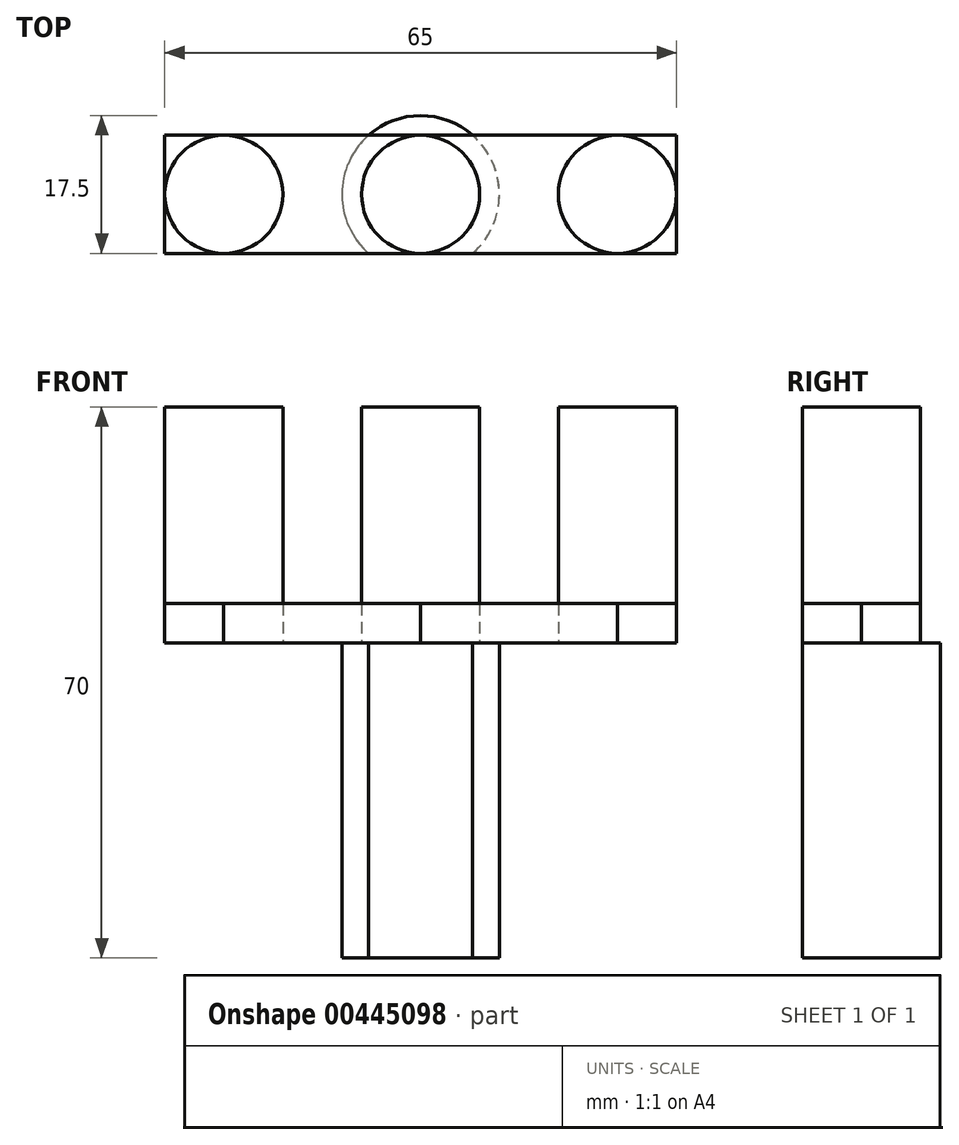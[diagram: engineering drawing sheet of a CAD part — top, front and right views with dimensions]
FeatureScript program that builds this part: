
annotation { "Feature Type Name" : "Feature", "Feature Type Description" : "" }
export const myFeature = defineFeature(function(context is Context, id is Id, definition is map)
    precondition{}
    {
        {
            var Q0;
            Q0=qCreatedBy(makeId("Top.planeOp"),FACE);
            var sketch = newSketch(context, id + "F0", { "sketchPlane" : qUnion([Q0])});
            skCircle(sketch, "E0", {"center": v(0, 0) * mm, "radius": 7.5 * mm});
            skCircle(sketch, "E1", {"center": v(-25, 0) * mm, "radius": 7.5 * mm});
            skCircle(sketch, "E2", {"center": v(25, 0) * mm, "radius": 7.5 * mm});
            skLineSegment(sketch, "E3.bottom", {"start": v(32.5, 7.5) * mm, "end": v(-32.5, 7.5) * mm});
            skLineSegment(sketch, "E3.top", {"start": v(32.5, -7.5) * mm, "end": v(-32.5, -7.5) * mm});
            skLineSegment(sketch, "E3.left", {"start": v(32.5, 7.5) * mm, "end": v(32.5, -7.5) * mm});
            skLineSegment(sketch, "E3.right", {"start": v(-32.5, 7.5) * mm, "end": v(-32.5, -7.5) * mm});
            skCircle(sketch, "E4", {"center": v(0, 0) * mm, "radius": 10 * mm});
            skSolve(sketch);
        }
        {
            var Q0;
            {var subQ0=sQuery(id+"F0.wireOp",EDGE,"E1");var subQ1=makeQuery(id+"F0.imprint","INTERSECT",VERTEX,{"derivedFrom":[subQ0,sQuery(id+"F0.wireOp",EDGE,"E3.right")]});Q0=makeQuery(id+"F0.imprint","IMPRINT",FACE,{"disambiguationData":[TD([[makeQuery(id+"F0.imprint","IMPRINT",EDGE,{"disambiguationData":[TD([[subQ1,1.0]])],"derivedFrom":subQ0}),1.0]])]});}
            var Q1;
            {var subQ0=sQuery(id+"F0.wireOp",EDGE,"E2");var subQ1=makeQuery(id+"F0.imprint","INTERSECT",VERTEX,{"derivedFrom":[subQ0,sQuery(id+"F0.wireOp",EDGE,"E3.bottom")]});Q1=makeQuery(id+"F0.imprint","IMPRINT",FACE,{"disambiguationData":[TD([[makeQuery(id+"F0.imprint","IMPRINT",EDGE,{"disambiguationData":[TD([[subQ1,1.0]])],"derivedFrom":subQ0}),1.0]])]});}
            var Q2;
            {var subQ0=sQuery(id+"F0.wireOp",EDGE,"E0");var subQ1=makeQuery(id+"F0.imprint","INTERSECT",VERTEX,{"derivedFrom":[subQ0,sQuery(id+"F0.wireOp",EDGE,"E3.bottom")]});Q2=makeQuery(id+"F0.imprint","IMPRINT",FACE,{"disambiguationData":[TD([[makeQuery(id+"F0.imprint","IMPRINT",EDGE,{"disambiguationData":[TD([[subQ1,-1.0]])],"derivedFrom":subQ0}),1.0]])]});}
            extrude(context, id + "F1", {"entities" : qUnion([Q0, Q1, Q2]), "depth" : 30 * mm});
        }
        {
            var Q0;
            {var subQ0=sQuery(id+"F0.wireOp",EDGE,"E3.bottom");var subQ1=sQuery(id+"F0.wireOp",EDGE,"E1");var subQ2=makeQuery(id+"F0.imprint","INTERSECT",VERTEX,{"derivedFrom":[subQ1,subQ0]});Q0=makeQuery(id+"F0.imprint","IMPRINT",FACE,{"disambiguationData":[TD([[makeQuery(id+"F0.imprint","IMPRINT",EDGE,{"disambiguationData":[TD([[subQ2,1.0]])],"derivedFrom":subQ1}),-1.0]])]});}
            var Q1;
            {var subQ0=sQuery(id+"F0.wireOp",EDGE,"E3.right");var subQ1=sQuery(id+"F0.wireOp",EDGE,"E1");var subQ2=makeQuery(id+"F0.imprint","INTERSECT",VERTEX,{"derivedFrom":[subQ1,subQ0]});Q1=makeQuery(id+"F0.imprint","IMPRINT",FACE,{"disambiguationData":[TD([[makeQuery(id+"F0.imprint","IMPRINT",EDGE,{"disambiguationData":[TD([[subQ2,-1.0]])],"derivedFrom":subQ1}),-1.0]])]});}
            var Q2;
            {var subQ0=sQuery(id+"F0.wireOp",EDGE,"E3.bottom");var subQ1=sQuery(id+"F0.wireOp",EDGE,"E0");var subQ2=makeQuery(id+"F0.imprint","INTERSECT",VERTEX,{"derivedFrom":[subQ1,subQ0]});Q2=makeQuery(id+"F0.imprint","IMPRINT",FACE,{"disambiguationData":[TD([[makeQuery(id+"F0.imprint","IMPRINT",EDGE,{"disambiguationData":[TD([[subQ2,-1.0]])],"derivedFrom":subQ1}),-1.0]])]});}
            var Q3;
            {var subQ0=sQuery(id+"F0.wireOp",EDGE,"E3.bottom");var subQ1=sQuery(id+"F0.wireOp",EDGE,"E0");var subQ2=makeQuery(id+"F0.imprint","INTERSECT",VERTEX,{"derivedFrom":[subQ1,subQ0]});Q3=makeQuery(id+"F0.imprint","IMPRINT",FACE,{"disambiguationData":[TD([[makeQuery(id+"F0.imprint","IMPRINT",EDGE,{"disambiguationData":[TD([[subQ2,1.0]])],"derivedFrom":subQ1}),-1.0]])]});}
            var Q4;
            {var subQ0=sQuery(id+"F0.wireOp",EDGE,"E3.bottom");var subQ1=sQuery(id+"F0.wireOp",EDGE,"E2");var subQ2=makeQuery(id+"F0.imprint","INTERSECT",VERTEX,{"derivedFrom":[subQ1,subQ0]});Q4=makeQuery(id+"F0.imprint","IMPRINT",FACE,{"disambiguationData":[TD([[makeQuery(id+"F0.imprint","IMPRINT",EDGE,{"disambiguationData":[TD([[subQ2,-1.0]])],"derivedFrom":subQ1}),-1.0]])]});}
            var Q5;
            {var subQ0=sQuery(id+"F0.wireOp",EDGE,"E3.left");var subQ1=sQuery(id+"F0.wireOp",EDGE,"E2");var subQ2=makeQuery(id+"F0.imprint","INTERSECT",VERTEX,{"derivedFrom":[subQ1,subQ0]});Q5=makeQuery(id+"F0.imprint","IMPRINT",FACE,{"disambiguationData":[TD([[makeQuery(id+"F0.imprint","IMPRINT",EDGE,{"disambiguationData":[TD([[subQ2,1.0]])],"derivedFrom":subQ1}),-1.0]])]});}
            var Q6;
            {var subQ0=sQuery(id+"F0.wireOp",EDGE,"E3.bottom");var subQ1=sQuery(id+"F0.wireOp",EDGE,"E2");var subQ2=makeQuery(id+"F0.imprint","INTERSECT",VERTEX,{"derivedFrom":[subQ1,subQ0]});Q6=makeQuery(id+"F0.imprint","IMPRINT",FACE,{"disambiguationData":[TD([[makeQuery(id+"F0.imprint","IMPRINT",EDGE,{"disambiguationData":[TD([[subQ2,1.0]])],"derivedFrom":subQ1}),-1.0]])]});}
            var Q7;
            {var subQ0=sQuery(id+"F0.wireOp",EDGE,"E3.right");var subQ1=sQuery(id+"F0.wireOp",EDGE,"E1");var subQ2=makeQuery(id+"F0.imprint","INTERSECT",VERTEX,{"derivedFrom":[subQ1,subQ0]});Q7=makeQuery(id+"F0.imprint","IMPRINT",FACE,{"disambiguationData":[TD([[makeQuery(id+"F0.imprint","IMPRINT",EDGE,{"disambiguationData":[TD([[subQ2,1.0]])],"derivedFrom":subQ1}),-1.0]])]});}
            extrude(context, id + "F2", {"entities" : qUnion([Q0, Q1, Q2, Q3, Q4, Q5, Q6, Q7]), "depth" : 5 * mm});
        }
        {
            var Q0;
            {var subQ0=sQuery(id+"F0.wireOp",EDGE,"E4");var subQ1=sQuery(id+"F0.wireOp",EDGE,"E3.top");var subQ2=makeQuery(id+"F0.imprint","INTERSECT",VERTEX,{"disambiguationData":[OD(0.0)],"derivedFrom":[subQ1,subQ0]});Q0=makeQuery(id+"F0.imprint","IMPRINT",FACE,{"disambiguationData":[TD([[makeQuery(id+"F0.imprint","IMPRINT",EDGE,{"disambiguationData":[TD([[subQ2,-1.0]])],"derivedFrom":subQ1}),1.0]])]});}
            var Q1;
            {var subQ0=sQuery(id+"F0.wireOp",EDGE,"E3.bottom");var subQ1=sQuery(id+"F0.wireOp",EDGE,"E0");var subQ2=makeQuery(id+"F0.imprint","INTERSECT",VERTEX,{"derivedFrom":[subQ1,subQ0]});Q1=makeQuery(id+"F0.imprint","IMPRINT",FACE,{"disambiguationData":[TD([[makeQuery(id+"F0.imprint","IMPRINT",EDGE,{"disambiguationData":[TD([[subQ2,-1.0]])],"derivedFrom":subQ1}),-1.0]])]});}
            var Q2;
            {var subQ0=sQuery(id+"F0.wireOp",EDGE,"E0");var subQ1=makeQuery(id+"F0.imprint","INTERSECT",VERTEX,{"derivedFrom":[subQ0,sQuery(id+"F0.wireOp",EDGE,"E3.bottom")]});Q2=makeQuery(id+"F0.imprint","IMPRINT",FACE,{"disambiguationData":[TD([[makeQuery(id+"F0.imprint","IMPRINT",EDGE,{"disambiguationData":[TD([[subQ1,-1.0]])],"derivedFrom":subQ0}),1.0]])]});}
            var Q3;
            {var subQ0=sQuery(id+"F0.wireOp",EDGE,"E4");var subQ1=sQuery(id+"F0.wireOp",EDGE,"E3.bottom");var subQ2=makeQuery(id+"F0.imprint","INTERSECT",VERTEX,{"disambiguationData":[OD(0.0)],"derivedFrom":[subQ1,subQ0]});Q3=makeQuery(id+"F0.imprint","IMPRINT",FACE,{"disambiguationData":[TD([[makeQuery(id+"F0.imprint","IMPRINT",EDGE,{"disambiguationData":[TD([[subQ2,-1.0]])],"derivedFrom":subQ1}),-1.0]])]});}
            var Q4;
            {var subQ0=sQuery(id+"F0.wireOp",EDGE,"E3.bottom");var subQ1=sQuery(id+"F0.wireOp",EDGE,"E0");var subQ2=makeQuery(id+"F0.imprint","INTERSECT",VERTEX,{"derivedFrom":[subQ1,subQ0]});Q4=makeQuery(id+"F0.imprint","IMPRINT",FACE,{"disambiguationData":[TD([[makeQuery(id+"F0.imprint","IMPRINT",EDGE,{"disambiguationData":[TD([[subQ2,1.0]])],"derivedFrom":subQ1}),-1.0]])]});}
            extrude(context, id + "F3", {"entities" : qUnion([Q0, Q1, Q2, Q3, Q4]), "oppositeDirection" : true, "depth" : 40 * mm});
        }
    });
